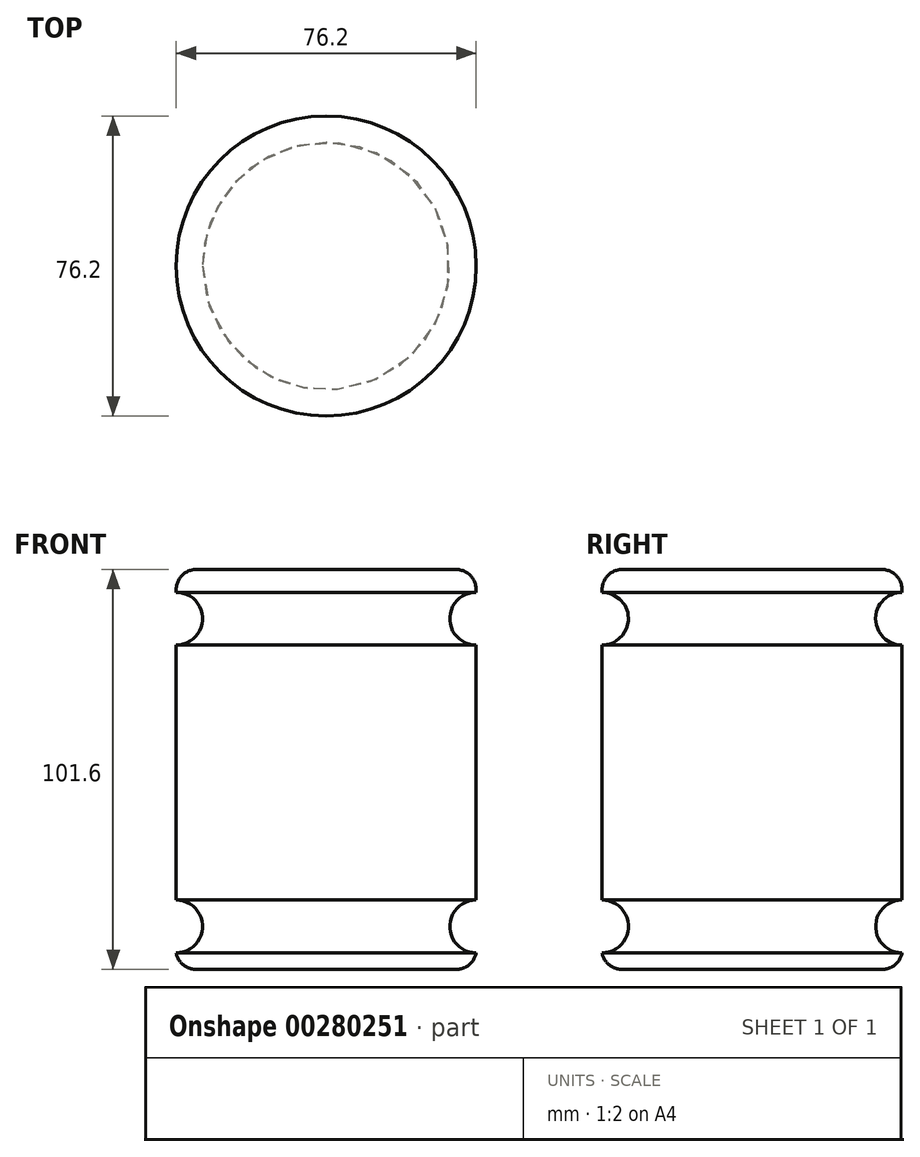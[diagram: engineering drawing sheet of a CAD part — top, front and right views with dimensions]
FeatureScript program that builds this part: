
annotation { "Feature Type Name" : "Feature", "Feature Type Description" : "" }
export const myFeature = defineFeature(function(context is Context, id is Id, definition is map)
    precondition{}
    {
        {
            var Q0;
            Q0=qCreatedBy(makeId("Front.planeOp"),FACE);
            var sketch = newSketch(context, id + "F0", { "sketchPlane" : qUnion([Q0])});
            skLineSegment(sketch, "E0.bottom", {"start": v(0, 0) * mm, "end": v(-38.1, 0) * mm});
            skLineSegment(sketch, "E0.top", {"start": v(0, 101.6) * mm, "end": v(-38.1, 101.6) * mm});
            skLineSegment(sketch, "E0.left", {"start": v(0, 0) * mm, "end": v(0, 101.6) * mm});
            skLineSegment(sketch, "E0.right", {"start": v(-38.1, 0) * mm, "end": v(-38.1, 101.6) * mm});
            skArc(sketch, "E1", {"start": v(0, 95.82) * mm, "mid": v(-6.7, 89.11) * mm, "end": v(0, 82.41) * mm});
            skArc(sketch, "E2", {"start": v(0, 17.62) * mm, "mid": v(-6.7, 10.92) * mm, "end": v(0, 4.21) * mm});
            skSolve(sketch);
        }
        {
            var Q0;
            {var subQ3=sQuery(id+"F0.wireOp",EDGE,"E0.bottom");Q0=makeQuery(id+"F0.imprint","IMPRINT",FACE,{"disambiguationData":[TD([[makeQuery(id+"F0.imprint","IMPRINT",EDGE,{"derivedFrom":subQ3}),-1.0]])]});}
            var Q1;
            Q1=sQuery(id+"F0.wireOp",EDGE,"E0.right");
            revolve(context, id + "F1", {"entities" : qUnion([Q0]), "axis" : qUnion([Q1]), "revolveType" : RevolveType.FULL});
        }
        {
            var Q0;
            Q0=makeQuery(id+"F1.opRevolve","SWEPT_EDGE",EDGE,{"disambiguationData":[OSD([sQuery(id+"F0.wireOp",EDGE,"E0.top"),sQuery(id+"F0.wireOp",EDGE,"E0.left")])]});
            var Q1;
            Q1=makeQuery(id+"F1.opRevolve","SWEPT_FACE",FACE,{"disambiguationData":[OSD([sQuery(id+"F0.wireOp",EDGE,"E0.bottom")])]});
            fillet(context, id + "F2", {"entities" : qUnion([Q0, Q1]), "radius" : 5.08 * mm, "tangentPropagation" : true, "allowEdgeOverflow" : false});
        }
    });
